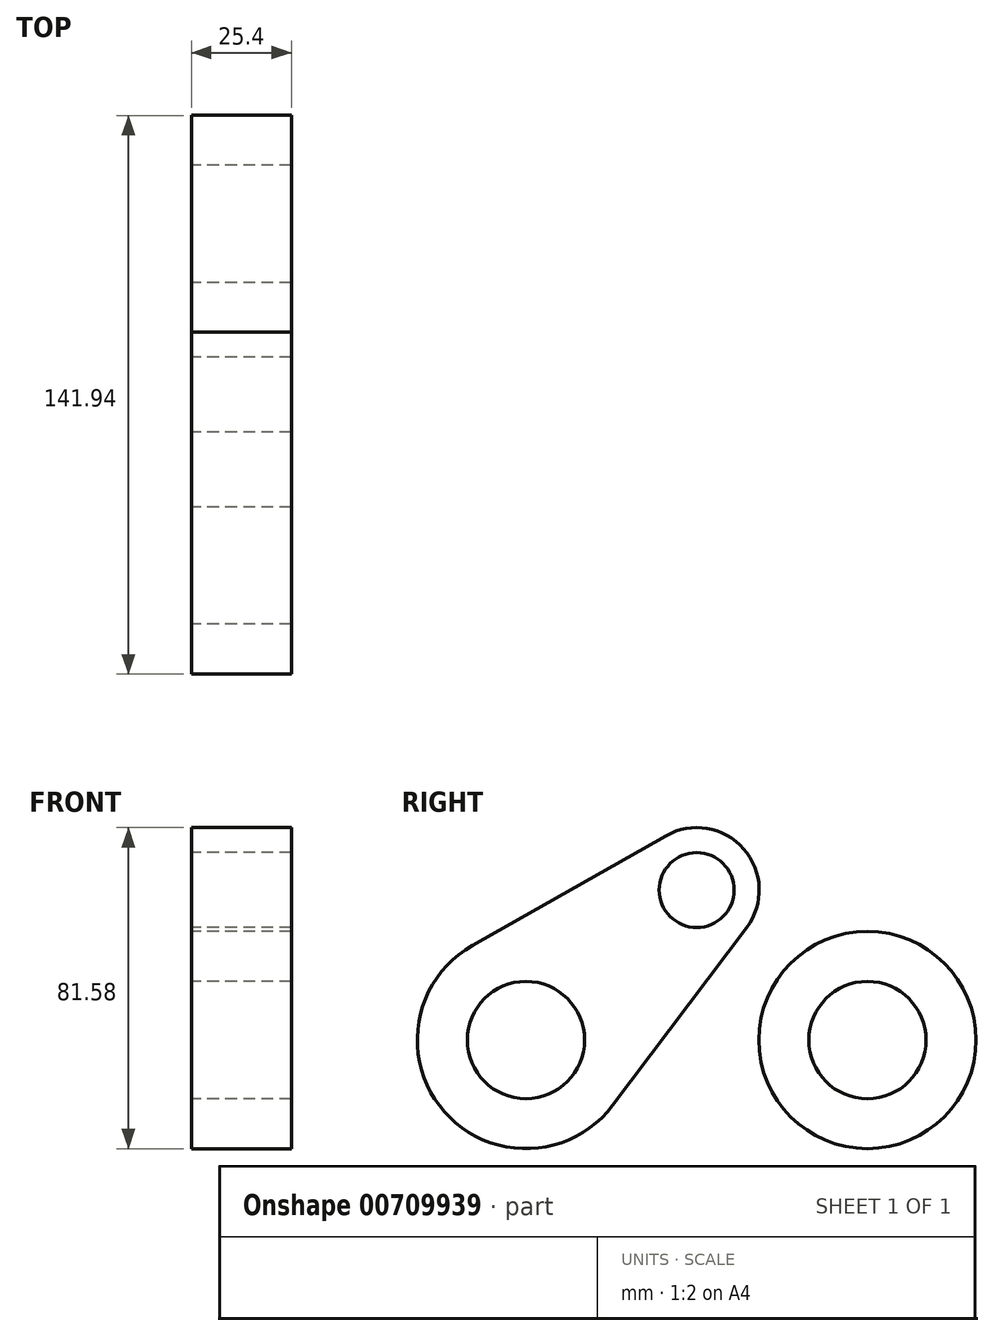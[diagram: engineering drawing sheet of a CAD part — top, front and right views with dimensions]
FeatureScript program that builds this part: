
annotation { "Feature Type Name" : "Feature", "Feature Type Description" : "" }
export const myFeature = defineFeature(function(context is Context, id is Id, definition is map)
    precondition{}
    {
        {
            var Q0;
            Q0=qCreatedBy(makeId("Right.planeOp"),FACE);
            var sketch = newSketch(context, id + "F0", { "sketchPlane" : qUnion([Q0])});
            skCircle(sketch, "E0", {"center": v(0, 38.1) * mm, "radius": 9.53 * mm});
            skCircle(sketch, "E1", {"center": v(43.38, 0) * mm, "radius": 14.9 * mm});
            skCircle(sketch, "E2.MirrorC", {"center": v(-43.38, 0) * mm, "radius": 14.9 * mm});
            skCircle(sketch, "E3.0", {"center": v(-43.38, 0) * mm, "radius": 27.6 * mm});
            skCircle(sketch, "E4.MirrorC", {"center": v(43.38, 0) * mm, "radius": 27.6 * mm});
            skCircle(sketch, "E5.0", {"center": v(0, 38.1) * mm, "radius": 15.87 * mm});
            skLineSegment(sketch, "E6", {"start": v(-57, 24) * mm, "end": v(-7.84, 51.9) * mm});
            skLineSegment(sketch, "E7", {"start": v(-21.34, -16.6) * mm, "end": v(12.68, 28.55) * mm});
            skSolve(sketch);
        }
        {
            var Q0;
            Q0 = qSketchRegion(id + "F0", true);
            extrude(context, id + "F1", {"entities" : qUnion([Q0]), "depth" : 25.4 * mm, "offsetDistance" : 25.4 * mm});
        }
    });
